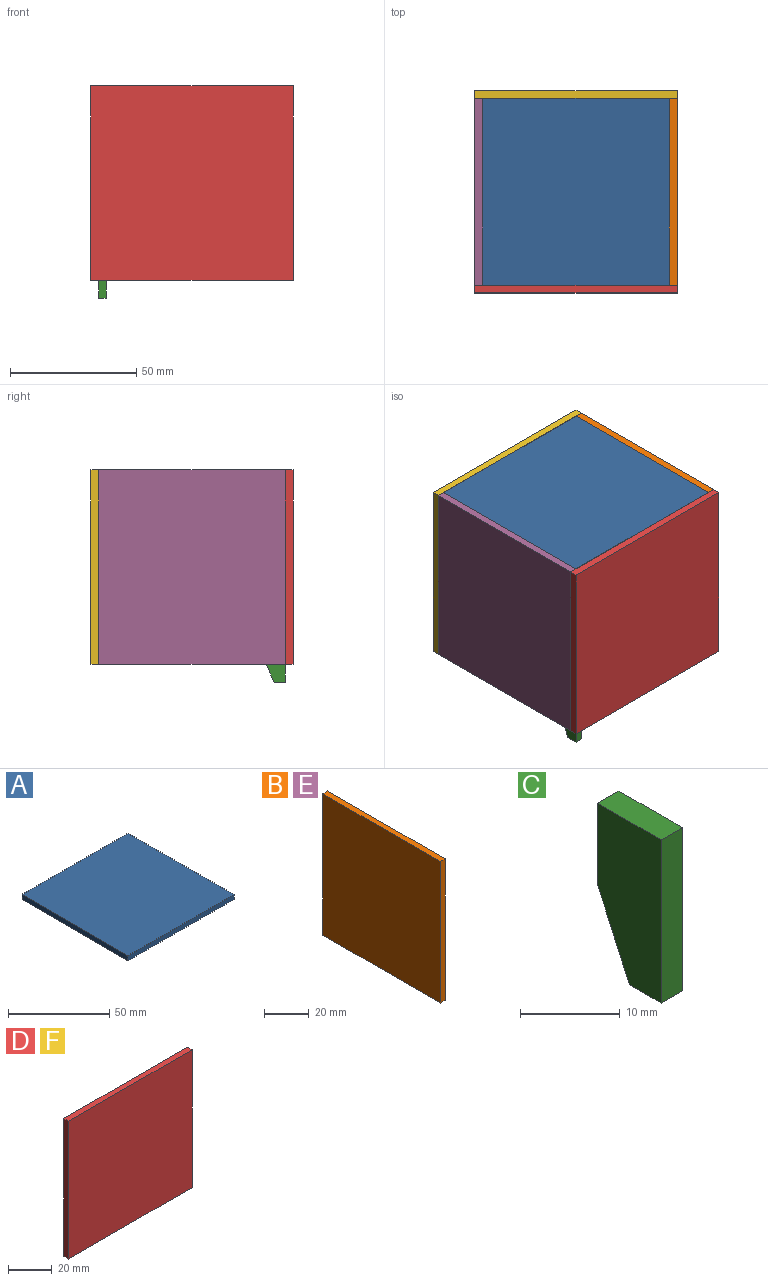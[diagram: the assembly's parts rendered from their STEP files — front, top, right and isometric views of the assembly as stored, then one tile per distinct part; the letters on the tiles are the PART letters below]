
ASSEMBLY  parts=6 mates=5
PART A: 6 faces, bbox 74x74x3 mm
  f0: plane 74x3mm, normal (-1,0,0), area 222mm2, adj f1,f3,f4,f5
  f1: plane 74x3mm, normal (0,1,0), area 222mm2, adj f0,f2,f4,f5
  f2: plane 74x3mm, normal (1,0,0), area 222mm2, adj f1,f3,f4,f5
  f3: plane 74x3mm, normal (0,-1,0), area 222mm2, adj f0,f2,f4,f5
  f4: plane 74x74mm, normal (0,0,1), area 5476mm2, adj f0,f1,f2,f3
  f5: plane 74x74mm, normal (0,0,-1), area 5476mm2, adj f0,f1,f2,f3
PART B: 6 faces, bbox 3x74x77 mm
  f0: plane 74x3mm, normal (0,0,1), area 222mm2, adj f1,f3,f4,f5
  f1: plane 77x3mm, normal (0,1,0), area 231mm2, adj f0,f2,f4,f5
  f2: plane 74x3mm, normal (0,0,-1), area 222mm2, adj f1,f3,f4,f5
  f3: plane 77x3mm, normal (0,-1,0), area 231mm2, adj f0,f2,f4,f5
  f4: plane 77x74mm, normal (-1,0,0), area 5698mm2, adj f0,f1,f2,f3
  f5: plane 77x74mm, normal (1,0,0), area 5698mm2, adj f0,f1,f2,f3
PART C: 7 faces, bbox 3x9x20 mm
  f0: plane 20x3mm, normal (0,-1,0), area 60mm2, adj f1,f4,f5,f6
  f1: plane 9x3mm, normal (0,0,1), area 27mm2, adj f0,f2,f5,f6
  f2: plane 10x3mm, normal (0,1,0), area 30mm2, adj f1,f3,f5,f6
  f3: plane 10x4.5mm, normal (0,0.91,-0.41), area 32.9mm2, adj f2,f4,f5,f6
  f4: plane 4.5x3mm, normal (0,0,-1), area 13.5mm2, adj f0,f3,f5,f6
  f5: plane 20x9mm, normal (-1,0,0), area 157.5mm2, adj f0,f1,f2,f3,f4
  f6: plane 20x9mm, normal (1,0,0), area 157.5mm2, adj f0,f1,f2,f3,f4
PART D: 6 faces, bbox 80x3x77 mm
  f0: plane 80x3mm, normal (0,0,-1), area 240mm2, adj f1,f3,f4,f5
  f1: plane 77x3mm, normal (1,0,0), area 231mm2, adj f0,f2,f4,f5
  f2: plane 80x3mm, normal (0,0,1), area 240mm2, adj f1,f3,f4,f5
  f3: plane 77x3mm, normal (-1,0,0), area 231mm2, adj f0,f2,f4,f5
  f4: plane 80x77mm, normal (0,-1,0), area 6160mm2, adj f0,f1,f2,f3
  f5: plane 80x77mm, normal (0,1,0), area 6160mm2, adj f0,f1,f2,f3
PART E: same geometry as B
PART F: same geometry as D
PLACE A t=(1,0.39,58.39)mm
PLACE B t=(78,0.39,-15.61)mm
PLACE C t=(-2,-2,-93.4)mm
PLACE D t=(1,0.39,-92.61)mm
PLACE E t=(1,0.39,-15.61)mm
PLACE F t=(1,77.39,-92.61)mm
MATE fastened A.f0 <-> E.f5  axis (-1,0,0) through (-36,-36.61,-12.61)mm
MATE fastened A.f2 <-> B.f4  axis (-1,0,0) through (38,-36.61,-12.61)mm
MATE fastened D.f5 <-> E.f3  axis (0,-1,0) through (-39,-36.61,-12.61)mm
MATE fastened E.f5 <-> C.f5  axis (1,0,0) through (-36,-36.61,-89.61)mm
MATE fastened F.f4 <-> E.f1  axis (0,-1,0) through (-39,37.39,-12.61)mm
